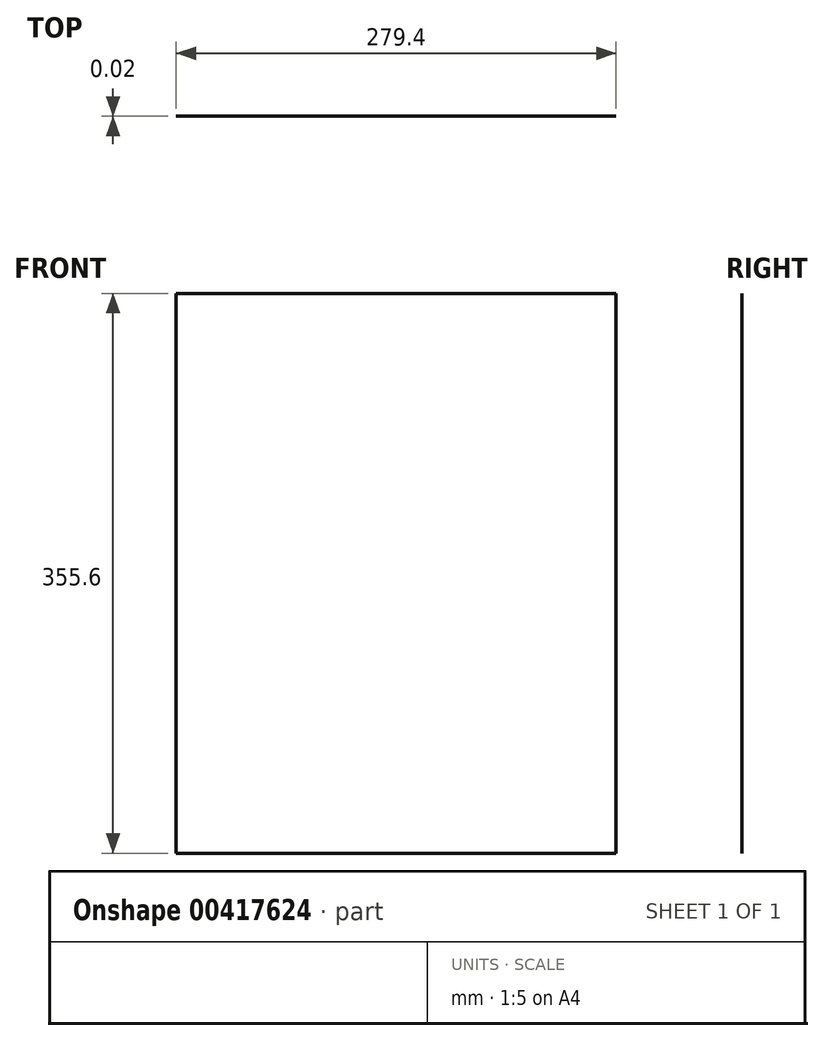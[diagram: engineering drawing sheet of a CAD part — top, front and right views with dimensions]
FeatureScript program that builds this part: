
annotation { "Feature Type Name" : "Feature", "Feature Type Description" : "" }
export const myFeature = defineFeature(function(context is Context, id is Id, definition is map)
    precondition{}
    {
        {
            var Q0;
            Q0=qCreatedBy(makeId("Front.planeOp"),FACE);
            var sketch = newSketch(context, id + "F0", { "sketchPlane" : qUnion([Q0])});
            skLineSegment(sketch, "E0.bottom", {"start": v(0, 0) * mm, "end": v(279.4, 0) * mm});
            skLineSegment(sketch, "E0.top", {"start": v(0, 355.6) * mm, "end": v(279.4, 355.6) * mm});
            skLineSegment(sketch, "E0.left", {"start": v(0, 0) * mm, "end": v(0, 355.6) * mm});
            skLineSegment(sketch, "E0.right", {"start": v(279.4, 0) * mm, "end": v(279.4, 355.6) * mm});
            skSolve(sketch);
        }
        {
            var Q0;
            Q0 = qSketchRegion(id + "F0", true);
            extrude(context, id + "F1", {"entities" : qUnion([Q0]), "depth" : 5 / 203.2 * mm});
        }
    });
